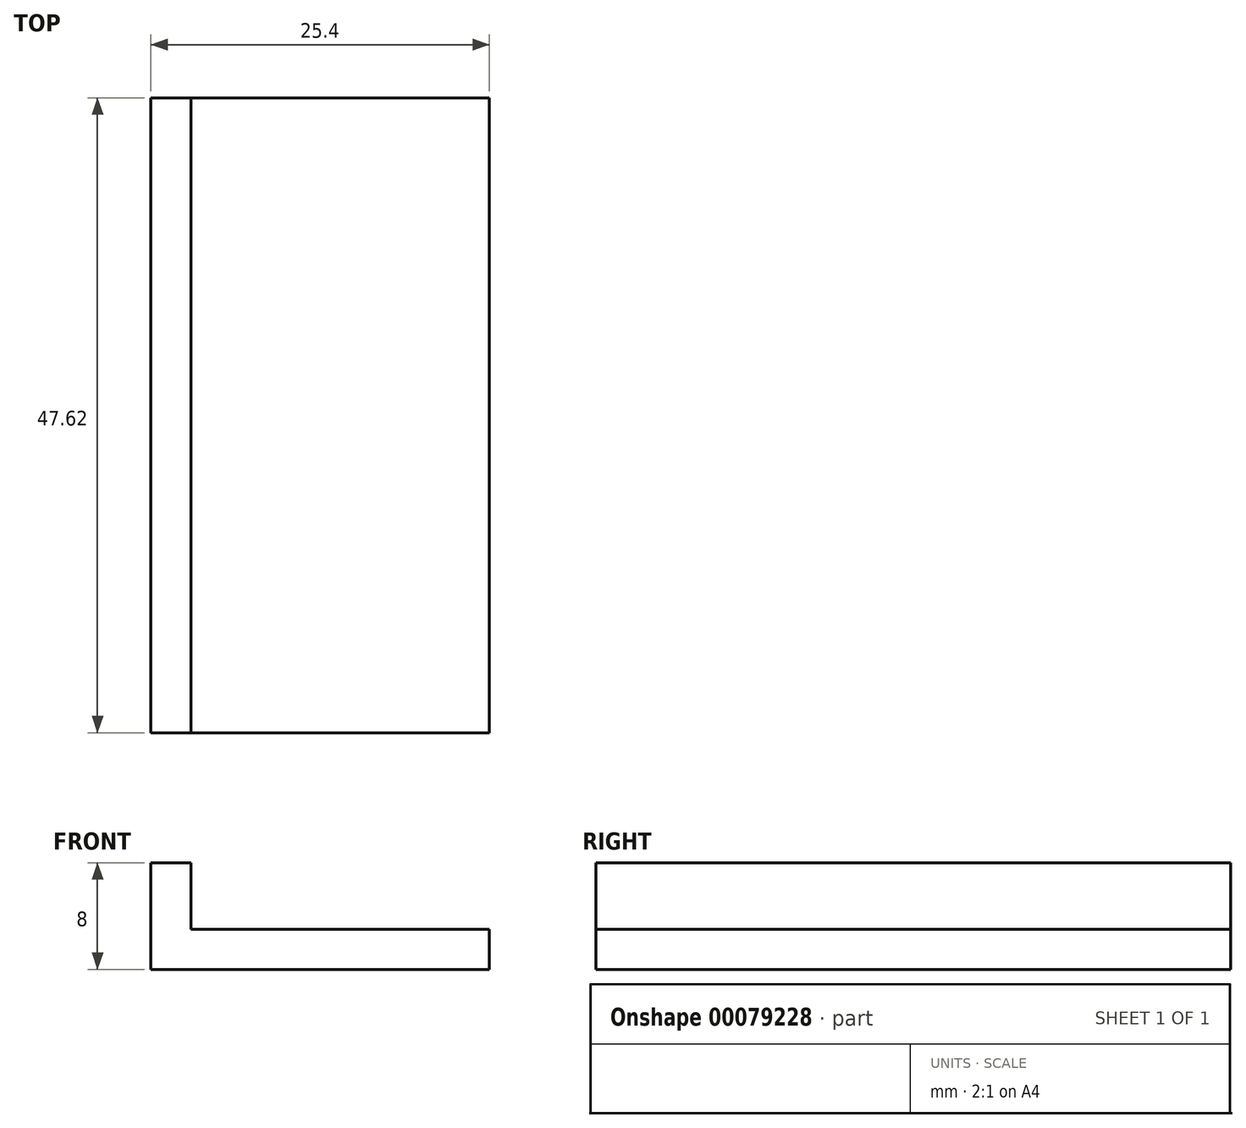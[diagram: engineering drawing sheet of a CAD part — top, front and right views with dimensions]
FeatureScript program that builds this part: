
annotation { "Feature Type Name" : "Feature", "Feature Type Description" : "" }
export const myFeature = defineFeature(function(context is Context, id is Id, definition is map)
    precondition{}
    {
        {
            var Q0;
            Q0=qCreatedBy(makeId("Top.planeOp"),FACE);
            var sketch = newSketch(context, id + "F0", { "sketchPlane" : qUnion([Q0])});
            skLineSegment(sketch, "E0.bottom", {"start": v(0, 0) * mm, "end": v(25.4, 0) * mm});
            skLineSegment(sketch, "E0.top", {"start": v(0, 47.62) * mm, "end": v(25.4, 47.62) * mm});
            skLineSegment(sketch, "E0.left", {"start": v(0, 0) * mm, "end": v(0, 47.62) * mm});
            skLineSegment(sketch, "E0.right", {"start": v(25.4, 0) * mm, "end": v(25.4, 47.62) * mm});
            skLineSegment(sketch, "E1", {"start": v(3, 47.63) * mm, "end": v(3, 0) * mm});
            skSolve(sketch);
        }
        {
            var Q0;
            Q0 = qSketchRegion(id + "F0", true);
            extrude(context, id + "F1", {"entities" : qUnion([Q0]), "depth" : 3 * mm});
        }
        {
            var Q0;
            {var subQ0=sQuery(id+"F0.wireOp",EDGE,"E0.left");Q0=makeQuery(id+"F0.imprint","IMPRINT",FACE,{"disambiguationData":[TD([[makeQuery(id+"F0.imprint","IMPRINT",EDGE,{"derivedFrom":subQ0}),-1.0]])]});}
            extrude(context, id + "F2", {"entities" : qUnion([Q0]), "operationType" : NewBodyOperationType.ADD, "depth" : 8 * mm});
        }
    });
